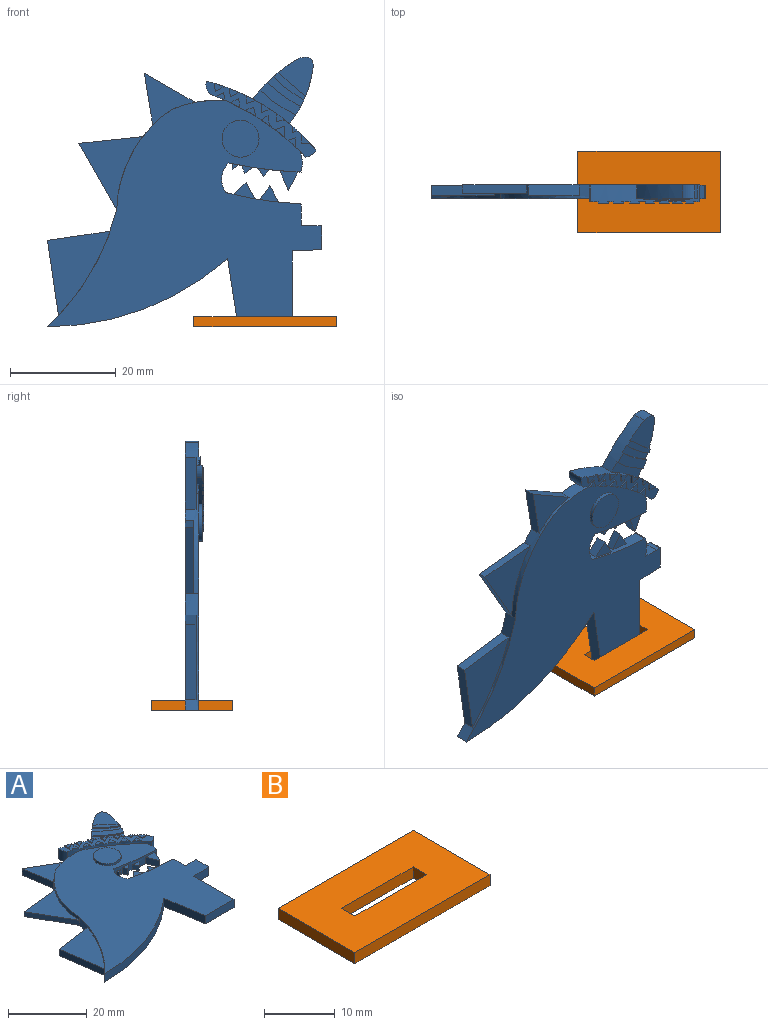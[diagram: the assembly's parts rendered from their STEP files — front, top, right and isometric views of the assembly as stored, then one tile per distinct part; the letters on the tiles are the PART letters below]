
ASSEMBLY  parts=2 mates=1
PART A: 108 faces, bbox 51.9x51x3.5 mm
  f0: cylinder r=40.43mm len=20.74mm, axis (0,0,-1), area 61.9mm2, adj f19,f50,f51,f52,f71,f72,f73,f74
  f1: cylinder r=75.63mm len=13.68mm, axis (0,0,-1), area 18.6mm2, adj f15,f16,f18,f19,f26,f27,f28,f29
  f2: cylinder r=23.83mm len=18.96mm, axis (0,0,-1), area 24.9mm2, adj f3,f4,f18,f19,f24,f25,f35,f37
  f3: cylinder r=21.41mm len=10.42mm, axis (0,0,-1), area 17.5mm2, adj f2,f18,f19,f23,f25,f49
  f4: cylinder r=45.35mm len=22.15mm, axis (0,0,-1), area 27.8mm2, adj f2,f5,f18,f19,f20,f21,f22,f36
  f5: cylinder r=51.5mm len=34.08mm, axis (0,0,-1), area 94.6mm2, adj f4,f6,f18,f19
  f6: plane 12.89x2.54mm, normal (-0.99,-0.15,0), area 33.1mm2, adj f5,f7,f18,f19
  f7: plane 10.26x2.54mm, normal (0,-1,0), area 26.1mm2, adj f6,f8,f18,f19
  f8: plane 14.37x2.54mm, normal (1,0,0), area 36.5mm2, adj f7,f9,f18,f19
  f9: plane 5.32x2.54mm, normal (0.04,-1,0), area 13.5mm2, adj f8,f18,f19,f105
  f10: plane 4.09x2.54mm, normal (1,0,0), area 10.4mm2, adj f18,f19,f105,f106
  f11: plane 2.54x0.83mm, normal (-0.1,0.99,0), area 2.1mm2, adj f12,f18,f19,f106
  f12: plane 2.81x2.54mm, normal (0,1,0), area 7.1mm2, adj f11,f13,f18,f19
  f13: cylinder r=25.4mm len=3.96mm, axis (0,0,-1), area 10.1mm2, adj f12,f18,f19,f107
  f14: cylinder r=63.35mm len=14mm, axis (0,0,-1), area 22mm2, adj f15,f18,f19,f32,f33,f34,f44,f45
  f15: cylinder r=4.2mm len=5.61mm, axis (0,0,-1), area 15.7mm2, adj f1,f14,f18,f19
  f16: cylinder r=6.4mm len=3.45mm, axis (0,0,-1), area 8.9mm2, adj f1,f17,f18,f19
  f17: cylinder r=12.91mm len=2.54mm, axis (0,0,-1), area 1.1mm2, adj f16,f18,f19,f49
  f18: plane 51.91x42.87mm, normal (0,0,1), area 1183mm2, adj f1,f2,f3,f4,f5,f6,f7,f8
  f19: plane 51.91x51.03mm, normal (0,0,-1), area 1584.1mm2, adj f0,f1,f2,f3,f4,f5,f6,f7
  f20: plane 14.3x2.08mm, normal (-0.99,-0.14,0), area 29.4mm2, adj f4,f19,f21,f22
  f21: plane 11.87x2.03mm, normal (-0.14,0.99,0), area 24.4mm2, adj f4,f19,f20,f22
  f22: plane 16.02x11.87mm, normal (0,0,1), area 98.9mm2, adj f4,f20,f21
  f23: plane 9.61x5.51mm, normal (0.5,0.87,0), area 22.5mm2, adj f3,f19,f24,f25
  f24: plane 9.83x2.03mm, normal (-0.99,-0.16,0), area 20.2mm2, adj f2,f19,f23,f25
  f25: plane 9.83x9.61mm, normal (0,0,1), area 37.9mm2, adj f2,f3,f23,f24
  f26: plane 2.03x1.47mm, normal (-0.92,-0.4,0), area 3.3mm2, adj f1,f19,f27,f28
  f27: plane 2.03x1.44mm, normal (0.61,-0.79,0), area 3.7mm2, adj f1,f19,f26,f28
  f28: plane 2.09x1.47mm, normal (0,0,1), area 1.4mm2, adj f1,f26,f27
  f29: plane 3.74x2.03mm, normal (-0.92,-0.39,0), area 8.3mm2, adj f1,f19,f30,f31
  f30: plane 3.52x2.03mm, normal (0.89,-0.45,0), area 8mm2, adj f1,f19,f29,f31
  f31: plane 3.74x3.39mm, normal (0,0,1), area 6.1mm2, adj f1,f29,f30
  f32: plane 2.43x2.22mm, normal (-0.67,0.74,0), area 6.7mm2, adj f14,f19,f33,f34
  f33: plane 3.07x2.03mm, normal (0.88,0.47,0), area 7.1mm2, adj f14,f19,f32,f34
  f34: plane 4.08x3.07mm, normal (0,0,1), area 5.7mm2, adj f14,f32,f33
  f35: plane 12.1x1.52mm, normal (-0.11,0.99,0), area 18.5mm2, adj f2,f19,f36,f37
  f36: plane 12.55x7.16mm, normal (-0.87,-0.5,0), area 22mm2, adj f4,f19,f35,f37
  f37: plane 13.83x12.1mm, normal (0,0,1), area 69.1mm2, adj f2,f35,f36
  f38: plane 1.52x1.01mm, normal (-1,0,0), area 1.5mm2, adj f1,f19,f39,f40
  f39: plane 1.52x1.21mm, normal (0.54,-0.84,0), area 2.2mm2, adj f1,f19,f38,f40
  f40: plane 1.21x1.01mm, normal (0,0,1), area 0.6mm2, adj f1,f38,f39
  f41: plane 1.52x1.51mm, normal (-0.82,-0.57,0), area 2.8mm2, adj f1,f19,f42,f43
  f42: plane 1.52x1.24mm, normal (0.74,-0.67,0), area 2.5mm2, adj f1,f19,f41,f43
  f43: plane 2.17x1.51mm, normal (0,0,1), area 1.5mm2, adj f1,f41,f42
  f44: plane 2.65x1.92mm, normal (-0.81,0.59,0), area 5mm2, adj f14,f19,f45,f46
  f45: plane 3.12x1.7mm, normal (0.88,0.48,0), area 5.4mm2, adj f14,f19,f44,f46
  f46: plane 3.63x3.12mm, normal (0,0,1), area 5.3mm2, adj f14,f44,f45
  f47: cylinder r=3.5mm len=7mm, axis (0,0,-1), area 14mm2, adj f18,f48
  f48: plane 7x7mm, normal (0,0,1), area 38.5mm2, adj f47
  f49: cylinder r=46.29mm len=18.3mm, axis (0,0,-1), area 30.5mm2, adj f3,f17,f18,f19,f50,f51,f52,f53
  f50: cylinder r=2.21mm len=3.18mm, axis (0,0,-1), area 7.9mm2, adj f0,f19,f49,f52
  f51: cylinder r=3.14mm len=3.18mm, axis (0,0,-1), area 8mm2, adj f0,f19,f49,f52
  f52: plane 20.8x14.4mm, normal (0,0,1), area 42.2mm2, adj f0,f49,f50,f51,f54,f55,f57,f58
  f53: plane 1.76x1.45mm, normal (0,0,1), area 1.3mm2, adj f49,f54,f55
  f54: plane 1.45x0.44mm, normal (-0.29,0.96,0), area 0.5mm2, adj f49,f52,f53,f55
  f55: plane 1.76x0.32mm, normal (1,0,0), area 0.6mm2, adj f49,f52,f53,f54
  f56: plane 2.06x1.71mm, normal (0,0,1), area 1.7mm2, adj f49,f57,f58
  f57: plane 1.71x0.69mm, normal (-0.38,0.93,0), area 0.6mm2, adj f49,f52,f56,f58
  f58: plane 2.06x0.32mm, normal (1,0,0), area 0.7mm2, adj f49,f52,f56,f57
  f59: plane 1.82x1.54mm, normal (0,0,1), area 1.3mm2, adj f49,f60,f61
  f60: plane 1.32x0.76mm, normal (-0.5,0.87,0), area 0.5mm2, adj f49,f52,f59,f61
  f61: plane 1.82x0.32mm, normal (0.99,0.12,0), area 0.6mm2, adj f49,f52,f59,f60
  f62: plane 1.96x1.73mm, normal (0,0,1), area 1.4mm2, adj f49,f63,f64
  f63: plane 1.51x0.58mm, normal (-0.36,0.93,0), area 0.5mm2, adj f49,f52,f62,f64
  f64: plane 1.73x0.45mm, normal (0.97,0.25,0), area 0.6mm2, adj f49,f52,f62,f63
  f65: plane 1.77x1.64mm, normal (0,0,1), area 1.3mm2, adj f49,f66,f67
  f66: plane 1.48x0.77mm, normal (-0.46,0.89,0), area 0.5mm2, adj f49,f52,f65,f67
  f67: plane 1.64x0.32mm, normal (0.98,0.18,0), area 0.5mm2, adj f49,f52,f65,f66
  f68: plane 1.44x0.32mm, normal (0.99,0.17,0), area 0.5mm2, adj f49,f52,f69,f70
  f69: plane 1.34x0.78mm, normal (-0.5,0.86,0), area 0.5mm2, adj f49,f52,f68,f70
  f70: plane 1.59x1.44mm, normal (0,0,1), area 1.1mm2, adj f49,f68,f69
  f71: plane 1.58x0.32mm, normal (-1,0,0), area 0.5mm2, adj f0,f52,f72,f73
  f72: plane 1.53x0.32mm, normal (0,-1,0), area 0.5mm2, adj f0,f52,f71,f73
  f73: plane 1.58x1.53mm, normal (0,0,1), area 1.2mm2, adj f0,f71,f72
  f74: plane 1.16x0.32mm, normal (-1,0,0), area 0.4mm2, adj f0,f52,f75,f76
  f75: plane 1.1x0.32mm, normal (0.15,-0.99,0), area 0.4mm2, adj f0,f52,f74,f76
  f76: plane 1.16x1.1mm, normal (0,0,1), area 0.6mm2, adj f0,f74,f75
  f77: plane 1.47x0.32mm, normal (-1,0,0), area 0.5mm2, adj f0,f52,f78,f79
  f78: plane 1.65x0.32mm, normal (0.14,-0.99,0), area 0.5mm2, adj f0,f52,f77,f79
  f79: plane 1.65x1.47mm, normal (0,0,1), area 1.2mm2, adj f0,f77,f78
  f80: plane 1.57x0.32mm, normal (-1,0,0), area 0.5mm2, adj f0,f52,f81,f82
  f81: plane 1.56x0.59mm, normal (0.36,-0.93,0), area 0.5mm2, adj f0,f52,f80,f82
  f82: plane 1.57x1.56mm, normal (0,0,1), area 1.2mm2, adj f0,f80,f81
  f83: plane 1.47x0.32mm, normal (-1,0,0), area 0.5mm2, adj f0,f52,f84,f85
  f84: plane 1.77x0.56mm, normal (0.3,-0.95,0), area 0.6mm2, adj f0,f52,f83,f85
  f85: plane 1.77x1.47mm, normal (0,0,1), area 1.3mm2, adj f0,f83,f84
  f86: plane 1.61x0.32mm, normal (-0.99,-0.11,0), area 0.5mm2, adj f0,f52,f87,f88
  f87: plane 1.58x0.88mm, normal (0.49,-0.87,0), area 0.6mm2, adj f0,f52,f86,f88
  f88: plane 1.75x1.61mm, normal (0,0,1), area 1.4mm2, adj f0,f86,f87
  f89: plane 1.58x0.32mm, normal (-0.99,-0.14,0), area 0.5mm2, adj f0,f52,f90,f91
  f90: plane 1.68x0.96mm, normal (0.5,-0.87,0), area 0.6mm2, adj f0,f52,f89,f91
  f91: plane 1.9x1.58mm, normal (0,0,1), area 1.4mm2, adj f0,f89,f90
  f92: cylinder r=30.21mm len=8.73mm, axis (0,0,-1), area 30.7mm2, adj f0,f19,f94,f95,f97,f98,f99,f100
  f93: cylinder r=22.41mm len=10.57mm, axis (0,0,-1), area 30.3mm2, adj f0,f19,f94,f95,f96,f98,f99,f100
  f94: plane 8.18x6.37mm, normal (0,0,1), area 14.5mm2, adj f0,f92,f93,f95
  f95: cylinder r=23.21mm len=6.79mm, axis (0,0,-1), area 2.6mm2, adj f92,f93,f94,f104
  f96: cylinder r=2.13mm len=2.54mm, axis (0,0,-1), area 4.9mm2, adj f19,f93,f97,f98
  f97: cylinder r=2.84mm len=2.54mm, axis (0,0,-1), area 5.9mm2, adj f19,f92,f96,f98
  f98: plane 7.41x6.66mm, normal (0,0,1), area 28.2mm2, adj f92,f93,f96,f97,f99
  f99: cylinder r=112.06mm len=5.15mm, axis (0,0,-1), area 2.2mm2, adj f92,f93,f98,f102
  f100: plane 6.91x5.7mm, normal (0,0,1), area 11.1mm2, adj f92,f93,f101,f103
  f101: cylinder r=20.67mm len=5.71mm, axis (0,0,-1), area 2.3mm2, adj f92,f93,f100,f102
  f102: plane 6.01x5.16mm, normal (0,0,1), area 7.7mm2, adj f92,f93,f99,f101
  f103: cylinder r=27.23mm len=6.29mm, axis (0,0,-1), area 2.5mm2, adj f92,f93,f100,f104
  f104: plane 7.69x6.14mm, normal (0,0,1), area 15.8mm2, adj f92,f93,f95,f103
  f105: cylinder r=0.25mm len=2.54mm, axis (0,0,1), area 1mm2, adj f9,f10,f18,f19
  f106: cylinder r=0.25mm len=2.54mm, axis (0,0,-1), area 1.1mm2, adj f10,f11,f18,f19
  f107: cylinder r=0.25mm len=2.54mm, axis (0,0,1), area 0.9mm2, adj f13,f14,f18,f19
PART B: 10 faces, bbox 27x15.4x1.9 mm
  f0: plane 14.29x1.91mm, normal (0,1,0), area 27.2mm2, adj f1,f7,f8,f9
  f1: plane 2.67x1.91mm, normal (1,0,0), area 5.1mm2, adj f0,f2,f8,f9
  f2: plane 14.29x1.91mm, normal (0,-1,0), area 27.2mm2, adj f1,f7,f8,f9
  f3: plane 26.99x1.91mm, normal (0,-1,0), area 51.4mm2, adj f4,f6,f8,f9
  f4: plane 15.37x1.91mm, normal (1,0,0), area 29.3mm2, adj f3,f5,f8,f9
  f5: plane 26.99x1.91mm, normal (0,1,0), area 51.4mm2, adj f4,f6,f8,f9
  f6: plane 15.37x1.91mm, normal (-1,0,0), area 29.3mm2, adj f3,f5,f8,f9
  f7: plane 2.67x1.91mm, normal (-1,0,0), area 5.1mm2, adj f0,f2,f8,f9
  f8: plane 26.99x15.37mm, normal (0,0,1), area 376.6mm2, adj f0,f1,f2,f3,f4,f5,f6,f7
  f9: plane 26.99x15.37mm, normal (0,0,-1), area 376.6mm2, adj f0,f1,f2,f3,f4,f5,f6,f7
PLACE A rot(axis=(1,0,0),90deg) t=(-19.91,-8.55,13.26)mm
PLACE B t=(-4.1,-9.82,-12.14)mm
MATE fastened A.f7 <-> B.f9  axis (0,0,-1) through (-4.1,-9.82,-12.14)mm
